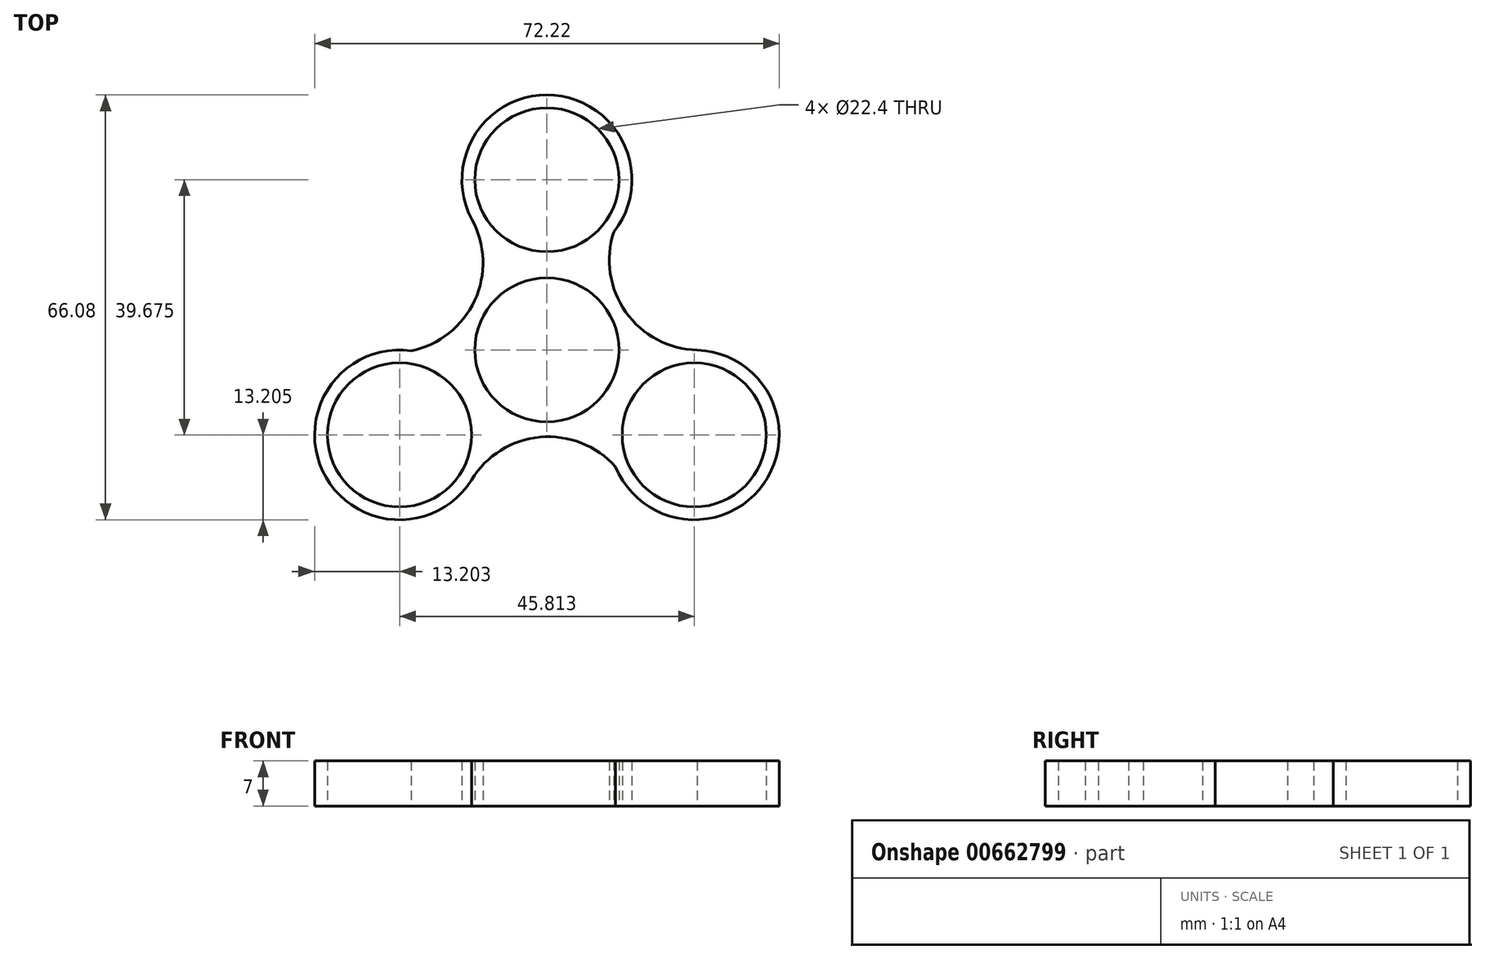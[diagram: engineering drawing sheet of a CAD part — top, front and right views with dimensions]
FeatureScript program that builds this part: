
annotation { "Feature Type Name" : "Feature", "Feature Type Description" : "" }
export const myFeature = defineFeature(function(context is Context, id is Id, definition is map)
    precondition{}
    {
        {
            var Q0;
            Q0=qCreatedBy(makeId("Top.planeOp"),FACE);
            var sketch = newSketch(context, id + "F0", { "sketchPlane" : qUnion([Q0])});
            skCircle(sketch, "E0", {"center": v(0, 0) * mm, "radius": 11.2 * mm});
            skCircle(sketch, "E1", {"center": v(0, 26.45) * mm, "radius": 11.2 * mm});
            skArc(sketch, "E2", {"start": v(10.41, 18.33) * mm, "mid": v(1.06, 39.6) * mm, "end": v(-11.57, 20.1) * mm});
            skArc(sketch, "E3.1.0", {"start": v(-21.08, -0.15) * mm, "mid": v(-34.83, -18.89) * mm, "end": v(-11.62, -20.07) * mm});
            skCircle(sketch, "E3.1.1", {"center": v(-22.9, -13.23) * mm, "radius": 11.2 * mm});
            skArc(sketch, "E3.2.0", {"start": v(10.67, -18.18) * mm, "mid": v(33.77, -20.72) * mm, "end": v(23.2, -0.03) * mm});
            skCircle(sketch, "E3.2.1", {"center": v(22.9, -13.23) * mm, "radius": 11.2 * mm});
            skArc(sketch, "E4", {"start": v(10.41, 18.33) * mm, "mid": v(12.26, 5.88) * mm, "end": v(23.38, -0.03) * mm});
            skArc(sketch, "E5.1.0", {"start": v(-21.08, -0.15) * mm, "mid": v(-11.23, 7.68) * mm, "end": v(-11.66, 20.26) * mm});
            skArc(sketch, "E5.2.0", {"start": v(10.67, -18.18) * mm, "mid": v(-1.04, -13.56) * mm, "end": v(-11.72, -20.23) * mm});
            skSolve(sketch);
        }
        {
            var Q0;
            Q0=makeQuery(id+"F0.imprint","IMPRINT",FACE,{"disambiguationData":[TD([[makeQuery(id+"F0.imprint","IMPRINT",EDGE,{"derivedFrom":sQuery(id+"F0.wireOp",EDGE,"E0")}),-1.0]])]});
            extrude(context, id + "F1", {"entities" : qUnion([Q0]), "depth" : 7 * mm, "offsetDistance" : 25 * mm});
        }
    });
